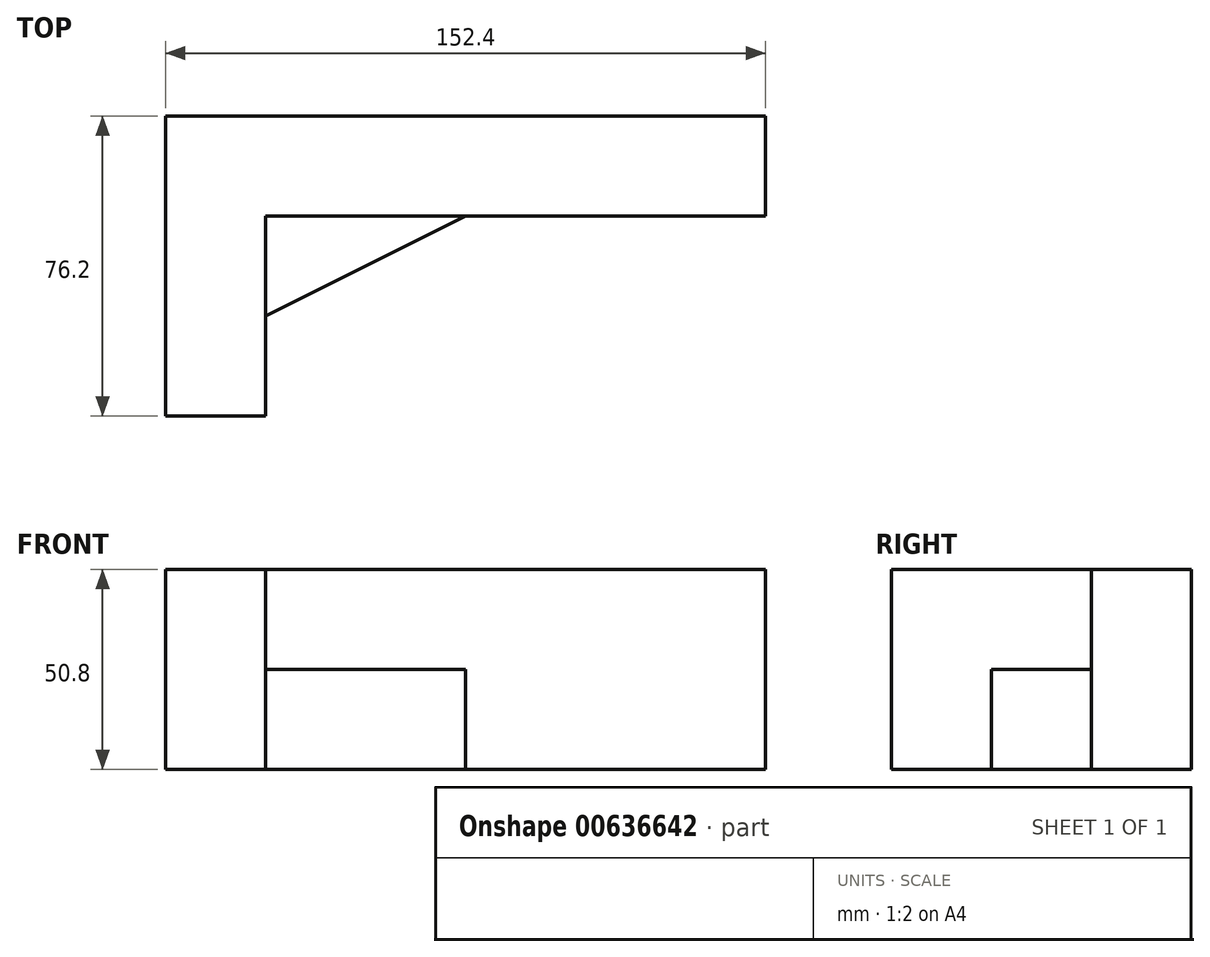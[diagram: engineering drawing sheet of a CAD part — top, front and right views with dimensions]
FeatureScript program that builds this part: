
annotation { "Feature Type Name" : "Feature", "Feature Type Description" : "" }
export const myFeature = defineFeature(function(context is Context, id is Id, definition is map)
    precondition{}
    {
        {
            var Q0;
            Q0=qCreatedBy(makeId("Top.planeOp"),FACE);
            var sketch = newSketch(context, id + "F0", { "sketchPlane" : qUnion([Q0])});
            skLineSegment(sketch, "E0", {"start": v(-25.78, -34.29) * mm, "end": v(-51.18, -34.29) * mm});
            skLineSegment(sketch, "E1", {"start": v(-51.18, -34.29) * mm, "end": v(-51.18, 41.91) * mm});
            skLineSegment(sketch, "E2", {"start": v(-51.18, 41.91) * mm, "end": v(101.22, 41.91) * mm});
            skLineSegment(sketch, "E3", {"start": v(101.22, 41.91) * mm, "end": v(101.22, 16.51) * mm});
            skLineSegment(sketch, "E4", {"start": v(-25.78, -34.29) * mm, "end": v(-25.78, 16.51) * mm});
            skLineSegment(sketch, "E5", {"start": v(-25.78, 16.51) * mm, "end": v(101.22, 16.51) * mm});
            skSolve(sketch);
        }
        {
            var Q0;
            Q0=makeQuery(id+"F0.imprint","IMPRINT",FACE,{"disambiguationData":[TD([[makeQuery(id+"F0.imprint","IMPRINT",EDGE,{"derivedFrom":sQuery(id+"F0.wireOp",EDGE,"E0")}),-1.0]])]});
            extrude(context, id + "F1", {"entities" : qUnion([Q0]), "depth" : 50.8 * mm, "offsetDistance" : 25.4 * mm});
        }
        {
            var Q0;
            Q0=makeQuery(id+"F1.opExtrude","CAP_FACE",FACE,{"disambiguationData":[OSD([sQuery(id+"F0.wireOp",EDGE,"E0"),sQuery(id+"F0.wireOp",EDGE,"E1"),sQuery(id+"F0.wireOp",EDGE,"E2"),sQuery(id+"F0.wireOp",EDGE,"E3"),sQuery(id+"F0.wireOp",EDGE,"E4"),sQuery(id+"F0.wireOp",EDGE,"E5")])],"isStart":true});
            var sketch = newSketch(context, id + "F2", { "sketchPlane" : qUnion([Q0])});
            skLineSegment(sketch, "E6", {"start": v(-25.78, -16.51) * mm, "end": v(-25.78, 8.89) * mm});
            skLineSegment(sketch, "E7", {"start": v(-25.78, -16.51) * mm, "end": v(25.02, -16.51) * mm});
            skLineSegment(sketch, "E8", {"start": v(-25.78, 8.89) * mm, "end": v(25.02, -16.51) * mm});
            skSolve(sketch);
        }
        {
            var Q0;
            Q0=makeQuery(id+"F2.imprint","IMPRINT",FACE,{"disambiguationData":[TD([[makeQuery(id+"F2.imprint","IMPRINT",EDGE,{"derivedFrom":sQuery(id+"F2.wireOp",EDGE,"E6")}),1.0]])]});
            extrude(context, id + "F3", {"entities" : qUnion([Q0]), "oppositeDirection" : true, "depth" : 25.4 * mm, "offsetDistance" : 25.4 * mm});
        }
    });
